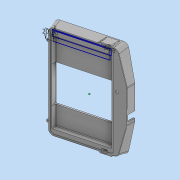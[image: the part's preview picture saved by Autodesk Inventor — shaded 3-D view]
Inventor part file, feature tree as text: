
AUTODESK INVENTOR PART (.ipt)
format: ipt  version: 2022 (Build 260153070, 153G)  size: 3,421,184 bytes
history: native  units: mm
features: other x53, plane x25, extrude x25, surface_op x22, sketch x21, fillet x9, draft x8, mirror x5, revolve x3, split x2, boolean_combine x2, loft x2, projected_geometry x2
ambient origin geometry x8: Origin, YZ Plane, XZ Plane, XY Plane, X Axis, Y Axis, Z Axis, Center Point
bodies: Solid5 (feature_tree), Solid6 (feature_tree), Solid15 (feature_tree), Solid16 (feature_tree), Solid10 (feature_tree)
feature tree (179):
  other  "P00173-09-002.ipt"
  other  "P00173-09-004.ipt"
  other  "P00173-09-003.ipt"
  other  "Blocks"
  plane  "Work Plane31"
  sketch  "Sketch56"  dims[d140=9.25mm d141=0.0mm d144=1.5mm]
  plane  "Work Plane5"
  plane  "Work Plane29"
  plane  "Work Plane - Screen_Mount_Side"
  plane  "Work Plane30"
  other  "Screen_Mount_Side"
  plane  "Work Plane25"
  plane  "Work Plane - Screen_Mount_Bottom"
  plane  "Work Plane34"
  sketch  "Sketch16"  dims[d159=0.349066mm d160=3.5mm d161=1.5mm d162=3.5mm d163=16.580628mm d165=3.5mm d166=2.0mm d167=28.0mm d168=55.0mm d169=0.349066mm d170=0.349066mm d171=0.2mm d53=360.0deg d54=360.0deg d55=2.5mm d56=8.0mm]
  plane  "Work Plane9"
  sketch  "Sketch21"  dims[d57=8.0mm d58=12.0mm]
  sketch  "Sketch58"  dims[d146=4.0mm d147=4.0mm]
  plane  "Work Plane33"
  plane  "Work Plane10"
  plane  "Work Plane11"
  sketch  "Sketch23"  dims[d59=0.0mm d60=0.0mm d92=5.0mm]
  plane  "Work Plane14"
  other  "Screen_Mount_1"
  other  "Screen_Mount_2"
  other  "Screen_Mount_3"
  sketch  "Sketch30"  dims[d105=20.674mm d106=0.174533mm d118=3.0mm]
  sketch  "Sketch29"  dims[d99=6.0mm d103=7.0mm d104=0.174533mm]
  plane  "Work Plane18"
  sketch  "Sketch33"  dims[d121=3.0mm d122=3.0mm d123=3.5mm]
  plane  "Work Plane20"
  sketch  "Sketch34"  dims[d128=1.0mm d129=1.0mm]
  plane  "Work Plane27"
  sketch  "Sketch53"  dims[d130=1.0mm d132=2.0mm]
  sketch  "Sketch54"  dims[d133=2.0mm d135=2.0mm]
  plane  "Work Plane28"
  sketch  "Sketch55"  dims[d136=4.0mm d137=0.0mm d138=2.0mm d139=0.0mm]
  other  "Privacy_Cover_Hook_Hole"
  sketch  "Sketch64"  dims[d158=1.5mm d164=10.0mm d172=0.087266mm]
  extrude  "Extrusion6"  Depth=10.0mm TaperAngle=0.0deg
  revolve  "Revolution3"  Angle=360.0deg
  surface_op  "Stitch Surface4"
  surface_op  "Extend1"
  surface_op  "Stitch Surface5"
  surface_op  "Extend2"
  fillet  "Fillet11"  [1 undecoded]
  fillet  "Fillet20"  Radius=2.5mm
  fillet  "Fillet21"  Radius=8.0mm
  surface_op  "Trim17"
  surface_op  "Trim18"
  surface_op  "Trim21"
  surface_op  "Trim22"
  surface_op  "Stitch Surface18"
  extrude  "Extrusion21"  Depth=12.0mm
  extrude  "Extrusion7"  Depth=5.0mm
  revolve  "Revolution1"  [1 undecoded]
  revolve  "Revolution2"  [1 undecoded]
  extrude  "Extrusion17"  Depth=3.0mm
  extrude  "Extrusion16"  Depth=3.0mm
  fillet  "Fillet19"  Radius=3.5mm
  split  "Split15"
  split  "Split16"
  mirror  "Mirror7"
  extrude  "Extrusion38"  Depth=1.0mm
  boolean_combine  "Combine2"
  extrude  "Extrusion22"  Depth=2.0mm
  extrude  "Extrusion8"  Depth=2.0mm
  extrude  "Extrusion29"  Depth=2.0mm TaperAngle=0.0deg
  extrude  "Extrusion36"  Depth=1.5mm
  extrude  "Extrusion39"  Depth=4.0mm
  mirror  "Mirror2"
  extrude  "Extrusion23"  Depth=4.0mm
  extrude  "Extrusion24"  Depth=0.3mm
  extrude  "Extrusion25"  Depth=2.0mm
  mirror  "Mirror3"
  extrude  "Extrusion26"  Depth=1.5mm
  extrude  "Extrusion27"  Depth=10.0mm
  mirror  "Mirror4"
  extrude  "Extrusion34"  Depth=2.0mm
  extrude  "Extrusion35"  Depth=2.0mm
  draft  "FaceDraft6"
  draft  "FaceDraft13"
  draft  "FaceDraft14"
  draft  "FaceDraft18"
  extrude  "Extrusion41"  Depth=2.0mm
  draft  "FaceDraft21"
  surface_op  "Trim23"
  surface_op  "Trim24"
  surface_op  "Trim25"
  surface_op  "Trim26"
  surface_op  "Stitch Surface20"
  draft  "FaceDraft22"
  extrude  "Extrusion42"  Depth=2.0mm
  fillet  "Fillet22"  Radius=15.7mm
  fillet  "Fillet23"  Radius=13.3mm
  extrude  "Extrusion43"  Depth=2.0mm
  extrude  "Extrusion44"  Depth=2.0mm
  boolean_combine  "Combine4"
  extrude  "Extrusion37"  Depth=10.0mm
  mirror  "Mirror6"
  fillet  "Fillet24"  Radius=2.0mm
  plane  "Work Plane - Cup_Draft"
  plane  "Work Plane - Cup_Draft_2"
  extrude  "Extrusion45"  Depth=2.0mm
  draft  "FaceDraft23"
  fillet  "Fillet25"  Radius=24.0mm
  draft  "FaceDraft24"
  fillet  "Fillet26"  Radius=25.0mm
  other  "Side"
  other  "Bottom"
  plane  "Work Plane1"
  other  "Top_Housing"
  other  "Screen_Hole"
  sketch  "Sketch10"  dims[d44=60.0mm d45=0.0mm]
  other  "USB_Hole_Top_Cover"
  other  "Top_Housing_Bottom_Edge"
  other  "Mount_Post"
  other  "USB_Position"
  plane  "Work Plane - TH_Bottom_Edge"
  plane  "Work Plane7"
  other  "Side_Camera"
  other  "Srf10"
  other  "Srf12"
  plane  "Work Plane - Screen_Top"
  other  "Srf13"
  other  "Srf14"
  other  "Srf15"
  other  "Fan_Side"
  other  "Fan_Front"
  other  "RPI"
  other  "PCB"
  other  "Camera_Top"
  other  "USB_Side"
  sketch  "Sketch25"  dims[d94=6.0mm d97=5.0mm]
  sketch  "Sketch29_1"  dims[d0=10.0mm d42=25.25mm d43=0.0mm]
  other  "USB_Cable_Opening"
  other  "USB_Cable_Opening_Rib"
  plane  "Work Plane _Opening"
  other  "Srf19"
  other  "Srf20"
  other  "Cover_Mount_Hole"
  sketch  "Sketch78"  dims[d173=10.0mm d174=-0.087266mm d175=0.3mm d178=2.0mm d93=85.0mm d96=49.0mm d98=58.0mm d180=15.7mm d181=13.3mm d182=2.0mm d183=12.0mm d184=10.0mm d185=0.087266mm d186=2.0mm d187=2.0mm d188=24.0mm d189=25.0mm d194=9.5mm d201=21.0mm d202=2.0mm d203=12.5mm d204=2.1mm d190=1.0mm d191=3.0mm d192=2.0mm d193=10.0mm d195=0.174533mm d196=0.2mm d197=0.2mm d198=90.0deg d199=10.0mm d200=10.0mm d225=10.0mm d227=1.0mm d228=0.0mm d229=90.0deg d230=0.0mm d231=90.0deg d232=1.0mm d234=0.0mm d235=90.0deg d236=0.0mm d237=90.0deg d238=1.0mm d241=5.25mm d242=5.5mm d253=15.882496mm d254=15.882496mm d257=12.0mm d264=10.0mm d265=0.174533mm d268=2.0mm d284=7.0mm d286=8.0mm d288=8.0mm d289=0.174533mm d311=10.0mm d316=5.0mm d317=2.0mm d318=3.0mm d319=2.0mm d320=2.0mm d321=3.0mm d322=0.1mm d323=3.0mm d325=0.5mm d326=1.0mm d327=0.174533mm d328=1.0mm d329=0.174533mm d330=2.792527mm d337=1.0mm d338=0.174533mm d339=2.792527mm d341=3.0mm d342=10.0mm d343=10.0mm d344=3.0mm d345=0.0mm d346=35.0mm d350=3.5mm d351=0.0mm d352=1.0mm d355=0.174533mm d357=1.0mm d358=1.0mm d359=8.0mm d360=10.0mm d361=2.0mm d363=2.0mm d364=0.2mm d365=2.0mm d367=0.5mm d368=8.0mm d369=0.5mm d372=1.0mm d373=20.0mm d374=0.0mm d375=0.0mm d380=2.0mm d381=0.0mm d382=2.0mm d387=10.0mm d388=0.0mm d389=1.5mm d391=20.0mm d392=2.0mm d393=2.0mm d394=1.0mm d395=1.0mm d398=5.0mm d399=0.0mm d400=0.436332mm d401=1.0mm d402=1.0mm d403=5.0mm d404=0.0mm d405=25.0mm d407=30.0mm d408=0.0mm d409=-0.523599mm d410=1.0mm d411=10.0mm d412=2.0mm d413=2.0mm d414=1.0mm d415=90.0deg d416=3.5mm d418=4.0mm d419=2.0mm d420=10.0mm d421=0.0mm d422=10.0mm d423=0.0mm d424=2.0mm d425=8.0mm d426=0.872665mm d427=0.872665mm d428=3.5mm d429=0.0mm d430=0.436332mm d431=2.0mm d432=0.0mm d433=0.872665mm d434=20.0mm d435=2.0mm d436=0.872665mm d437=2.0mm d73=0.5mm d74=0.872665mm d75=0.5mm d76=0.872665mm d370=0.5mm d371=0.872665mm]
  other  "Cover_Mount"
  other  "Solid10::P00173-09-003.ipt"
  other  "TaggingFeature2"
  plane  "Work Plane - Mount_Post"
  sketch  "Sketch60"  dims[d148=4.0mm d149=4.0mm]
  other  "Srf37"
  other  "Srf38"
  sketch  "Sketch61"  dims[d150=6.0mm d151=0.0mm d152=0.3mm]
  other  "Srf39"
  surface_op  "Stitch Surface17"
  other  "Srf42"
  other  "Srf43"
  other  "Srf44"
  sketch  "Sketch62"  dims[d153=0.3mm d155=2.0mm]
  other  "Srf45"
  surface_op  "Stitch Surface19"
  other  "Srf46"
  other  "Srf47"
  sketch  "Sketch63"  dims[d156=1.5mm d157=1.5mm]
  loft  "LoftSrf5"
  loft  "LoftSrf6"
  extrude  "ExtrusionSrf2"  Depth=2.0mm
  other  "OffsetSrf3"
  other  "OffsetSrf4"
  other  "Block2:1"
  other  "Block2:2"
  other  "RPI:1"
  other  "Camera_Top:1"
  other  "Srf34::Derived"
  projected_geometry  "Project Cut Edges1"
  surface_op  "Boundary Patch10"
  projected_geometry  "Project Cut Edges2"
  surface_op  "Boundary Patch12"
  surface_op  "Boundary Patch4"
  surface_op  "Boundary Patch8"
  surface_op  "Boundary Patch11"
  surface_op  "Boundary Patch3"
note: 3 required parameter values undecoded (feature->parameter linkage not recoverable at this tier; creation-order binding heuristic only, values carry confidence <= 0.55)